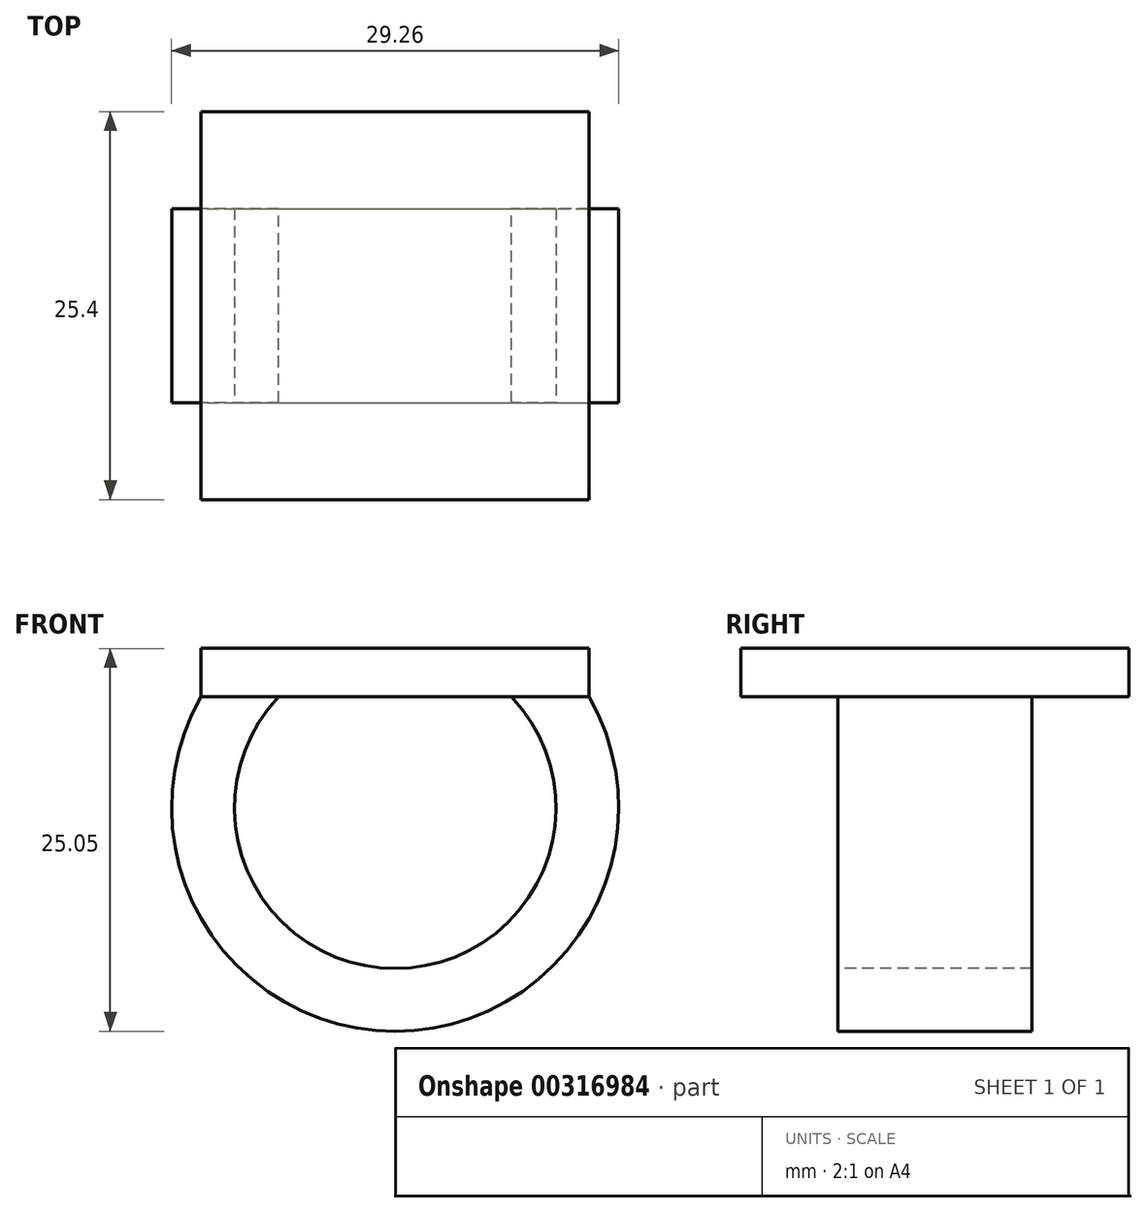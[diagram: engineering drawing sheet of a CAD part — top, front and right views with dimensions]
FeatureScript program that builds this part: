
annotation { "Feature Type Name" : "Feature", "Feature Type Description" : "" }
export const myFeature = defineFeature(function(context is Context, id is Id, definition is map)
    precondition{}
    {
        {
            var Q0;
            Q0=qCreatedBy(makeId("Top.planeOp"),FACE);
            var sketch = newSketch(context, id + "F0", { "sketchPlane" : qUnion([Q0])});
            skLineSegment(sketch, "E0.bottom", {"start": v(12.7, 12.7) * mm, "end": v(-12.7, 12.7) * mm});
            skLineSegment(sketch, "E0.top", {"start": v(12.7, -12.7) * mm, "end": v(-12.7, -12.7) * mm});
            skLineSegment(sketch, "E0.left", {"start": v(12.7, 12.7) * mm, "end": v(12.7, -12.7) * mm});
            skLineSegment(sketch, "E0.right", {"start": v(-12.7, 12.7) * mm, "end": v(-12.7, -12.7) * mm});
            skPoint(sketch, "E0.middle", {"position": v(0, 0) * mm});
            skSolve(sketch);
        }
        {
            var Q0;
            Q0 = qSketchRegion(id + "F0", true);
            extrude(context, id + "F1", {"entities" : qUnion([Q0]), "depth" : 3.17 * mm});
        }
        {
            var Q0;
            Q0=qCreatedBy(makeId("Front.planeOp"),FACE);
            var sketch = newSketch(context, id + "F2", { "sketchPlane" : qUnion([Q0])});
            skArc(sketch, "E1", {"start": v(-10.16, 0) * mm, "mid": v(0, -19.74) * mm, "end": v(10.16, 0) * mm});
            skSolve(sketch);
        }
        {
            var Q0;
            Q0=makeQuery(id+"F1.opExtrude","CAP_FACE",FACE,{"disambiguationData":[OSD([sQuery(id+"F0.wireOp",EDGE,"E0.bottom"),sQuery(id+"F0.wireOp",EDGE,"E0.top"),sQuery(id+"F0.wireOp",EDGE,"E0.left"),sQuery(id+"F0.wireOp",EDGE,"E0.right")])],"isStart":true});
            var sketch = newSketch(context, id + "F3", { "sketchPlane" : qUnion([Q0])});
            skLineSegment(sketch, "E2.bottom", {"start": v(-7.62, 6.35) * mm, "end": v(-12.7, 6.35) * mm});
            skLineSegment(sketch, "E2.top", {"start": v(-7.62, -6.35) * mm, "end": v(-12.7, -6.35) * mm});
            skLineSegment(sketch, "E2.left", {"start": v(-7.62, 6.35) * mm, "end": v(-7.62, -6.35) * mm});
            skLineSegment(sketch, "E2.right", {"start": v(-12.7, 6.35) * mm, "end": v(-12.7, -6.35) * mm});
            skPoint(sketch, "E2.middle", {"position": v(-10.16, 0) * mm});
            skSolve(sketch);
        }
        {
            var Q0;
            Q0 = qSketchRegion(id + "F3", true);
            var Q1;
            Q1 = qConstructionFilter(qBodyType(qCreatedBy(id + "F2" ,EDGE), BodyType.WIRE), ConstructionObject.NO);
            sweep(context, id + "F4", {"operationType" : NewBodyOperationType.ADD, "profiles" : qUnion([Q0]), "path" : qUnion([Q1])});
        }
        {
            var Q0;
            Q0=qCreatedBy(makeId("Front.planeOp"),FACE);
            var sketch = newSketch(context, id + "F5", { "sketchPlane" : qUnion([Q0])});
            skLineSegment(sketch, "E3.0", {"start": v(10.16, 0) * mm, "end": v(7.62, 0) * mm});
            skLineSegment(sketch, "E3.1", {"start": v(9.34, -2.4) * mm, "end": v(10.16, 0) * mm});
            skArc(sketch, "E3.2", {"start": v(9.34, -2.4) * mm, "mid": v(8.56, -1.14) * mm, "end": v(7.62, 0) * mm});
            skLineSegment(sketch, "E4.trimOffspring", {"start": v(-7.62, 0) * mm, "end": v(-12.7, 0) * mm});
            skPoint(sketch, "E5.orphan", {"position": v(12.7, 0) * mm});
            skSolve(sketch);
        }
        {
            var Q0;
            Q0 = qSketchRegion(id + "F5", true);
            var Q1;
            Q1=makeQuery(id+"F4.opSweep","SWEPT_FACE",FACE,{"disambiguationData":[OSD([sQuery(id+"F2.wireOp",EDGE,"E1"),sQuery(id+"F3.wireOp",EDGE,"E2.bottom")])]});
            var Q2;
            Q2=makeQuery(id+"F4.opSweep","SWEPT_FACE",FACE,{"disambiguationData":[OSD([sQuery(id+"F2.wireOp",EDGE,"E1"),sQuery(id+"F3.wireOp",EDGE,"E2.top")])]});
            extrude(context, id + "F6", {"entities" : qUnion([Q0]), "operationType" : NewBodyOperationType.ADD, "endBound" : BoundingType.UP_TO_SURFACE, "endBoundEntityFace" : qUnion([Q1]), "depth" : 25.4 * mm, "hasSecondDirection" : true, "secondDirectionBound" : SecondDirectionBoundingType.UP_TO_SURFACE, "secondDirectionOppositeDirection" : true, "secondDirectionBoundEntityFace" : qUnion([Q2]), "secondDirectionDepth" : 25.4 * mm});
        }
    });
